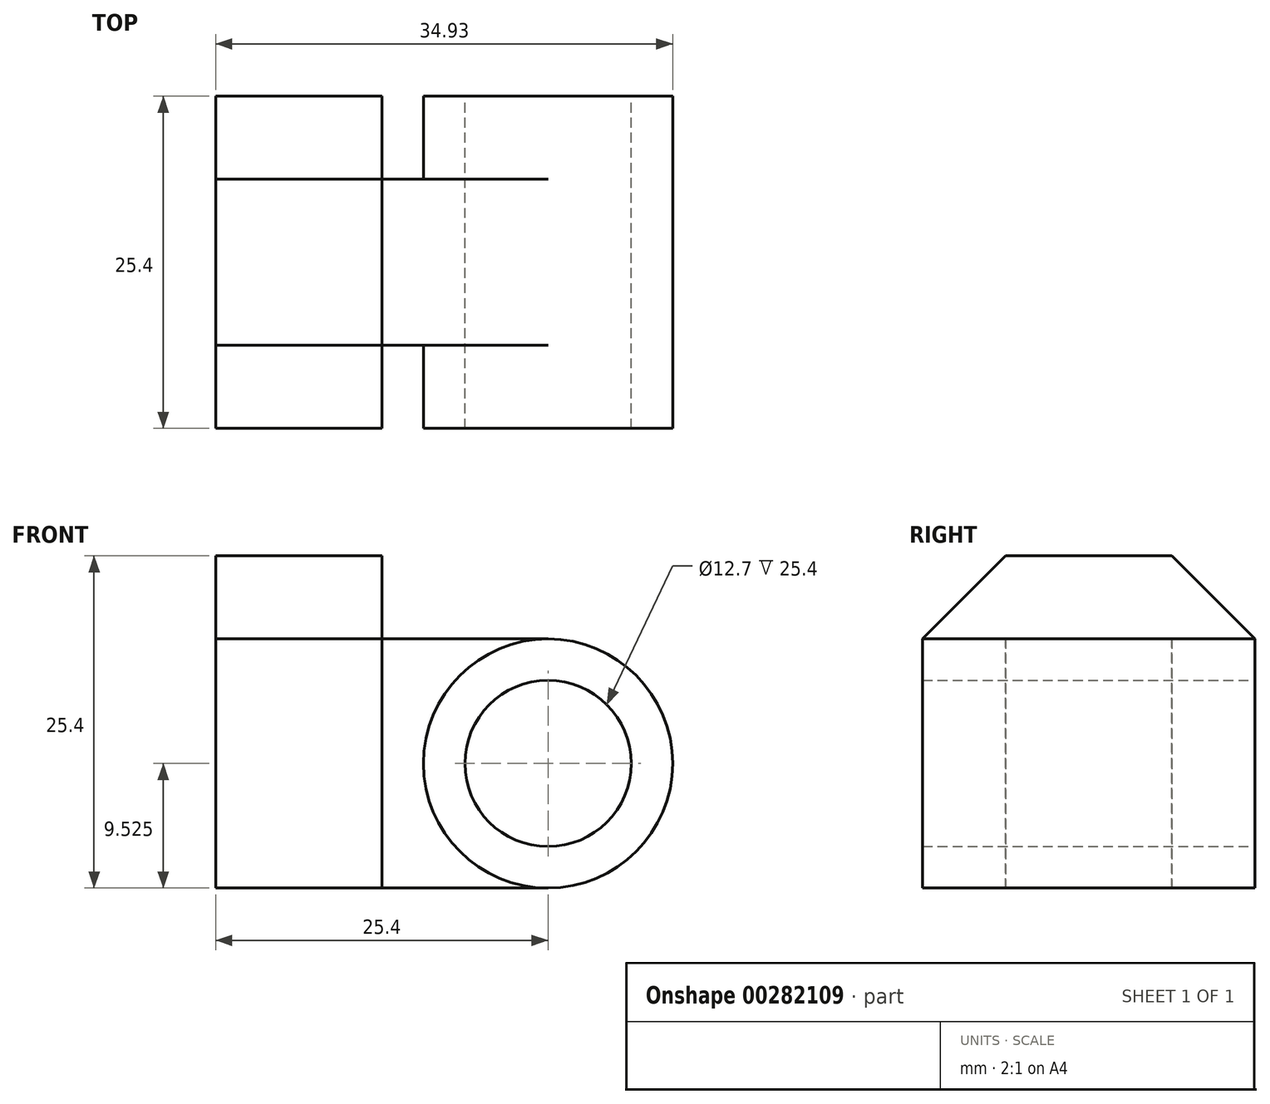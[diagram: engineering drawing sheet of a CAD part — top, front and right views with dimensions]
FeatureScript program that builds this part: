
annotation { "Feature Type Name" : "Feature", "Feature Type Description" : "" }
export const myFeature = defineFeature(function(context is Context, id is Id, definition is map)
    precondition{}
    {
        {
            var Q0;
            Q0=qCreatedBy(makeId("Right.planeOp"),FACE);
            var sketch = newSketch(context, id + "F0", { "sketchPlane" : qUnion([Q0])});
            skLineSegment(sketch, "E0", {"start": v(0, 25.4) * mm, "end": v(0, -25.4) * mm, "construction": true});
            skLineSegment(sketch, "E1", {"start": v(-25.4, 0) * mm, "end": v(25.4, 0) * mm, "construction": true});
            skLineSegment(sketch, "E2", {"start": v(-12.7, 0) * mm, "end": v(12.7, 0) * mm});
            skLineSegment(sketch, "E3", {"start": v(12.7, 0) * mm, "end": v(12.7, 19.05) * mm});
            skLineSegment(sketch, "E4", {"start": v(12.7, 19.05) * mm, "end": v(6.35, 25.4) * mm});
            skLineSegment(sketch, "E5", {"start": v(6.35, 25.4) * mm, "end": v(-6.35, 25.4) * mm});
            skLineSegment(sketch, "E6", {"start": v(-6.35, 25.4) * mm, "end": v(-12.7, 19.05) * mm});
            skLineSegment(sketch, "E7", {"start": v(-12.7, 19.05) * mm, "end": v(-12.7, 0) * mm});
            skSolve(sketch);
        }
        {
            var Q0;
            Q0 = qSketchRegion(id + "F0", true);
            extrude(context, id + "F1", {"entities" : qUnion([Q0]), "depth" : 12.7 * mm});
        }
        {
            var Q0;
            Q0=makeQuery(id+"F1.opExtrude","CAP_FACE",FACE,{"disambiguationData":[OSD([sQuery(id+"F0.wireOp",EDGE,"E2"),sQuery(id+"F0.wireOp",EDGE,"E3"),sQuery(id+"F0.wireOp",EDGE,"E4"),sQuery(id+"F0.wireOp",EDGE,"E5"),sQuery(id+"F0.wireOp",EDGE,"E6"),sQuery(id+"F0.wireOp",EDGE,"E7")])],"isStart":false});
            var sketch = newSketch(context, id + "F2", { "sketchPlane" : qUnion([Q0])});
            skLineSegment(sketch, "E8", {"start": v(-6.35, 0) * mm, "end": v(-6.35, 19.05) * mm});
            skLineSegment(sketch, "E9", {"start": v(-6.35, 19.05) * mm, "end": v(6.35, 19.05) * mm});
            skLineSegment(sketch, "E10", {"start": v(6.35, 19.05) * mm, "end": v(6.35, 0) * mm});
            skLineSegment(sketch, "E11", {"start": v(0, 25.4) * mm, "end": v(0, -25.4) * mm, "construction": true});
            skLineSegment(sketch, "E12", {"start": v(-25.4, 0) * mm, "end": v(25.4, 0) * mm, "construction": true});
            skSolve(sketch);
        }
        {
            var Q0;
            {var subQ0=sQuery(id+"F2.wireOp",EDGE,"E8");Q0=makeQuery(id+"F2.imprint","IMPRINT",FACE,{"disambiguationData":[TD([[makeQuery(id+"F2.imprint","IMPRINT",EDGE,{"derivedFrom":subQ0}),-1.0]])]});}
            extrude(context, id + "F3", {"entities" : qUnion([Q0]), "operationType" : NewBodyOperationType.ADD, "depth" : 12.7 * mm});
        }
        {
            var Q0;
            Q0=qCreatedBy(makeId("Front.planeOp"),FACE);
            var sketch = newSketch(context, id + "F4", { "sketchPlane" : qUnion([Q0])});
            skCircle(sketch, "E13", {"center": v(25.4, 9.53) * mm, "radius": 9.53 * mm});
            skCircle(sketch, "E14", {"center": v(25.4, 9.53) * mm, "radius": 6.35 * mm});
            skSolve(sketch);
        }
        {
            var Q0;
            Q0 = qSketchRegion(id + "F4", true);
            extrude(context, id + "F5", {"entities" : qUnion([Q0]), "operationType" : NewBodyOperationType.ADD, "endBound" : BoundingType.SYMMETRIC, "depth" : 25.4 * mm});
        }
        {
            var Q0;
            {var subQ0=sQuery(id+"F2.wireOp",EDGE,"E8");Q0=makeQuery(id+"F5.boolean.opBoolean","SPLIT",FACE,{"disambiguationData":[TD([makeQuery(id+"F5.opExtrude","SWEPT_FACE",FACE,{"disambiguationData":[OSD([sQuery(id+"F4.wireOp",EDGE,"E14")])]})])],"derivedFrom":makeQuery(id+"F3.opExtrude","SWEPT_FACE",FACE,{"disambiguationData":[OSD([subQ0])]})});}
            extrude(context, id + "F6", {"entities" : qUnion([Q0]), "operationType" : NewBodyOperationType.REMOVE, "endBound" : BoundingType.SYMMETRIC, "oppositeDirection" : true, "depth" : 25.4 * mm});
        }
    });
